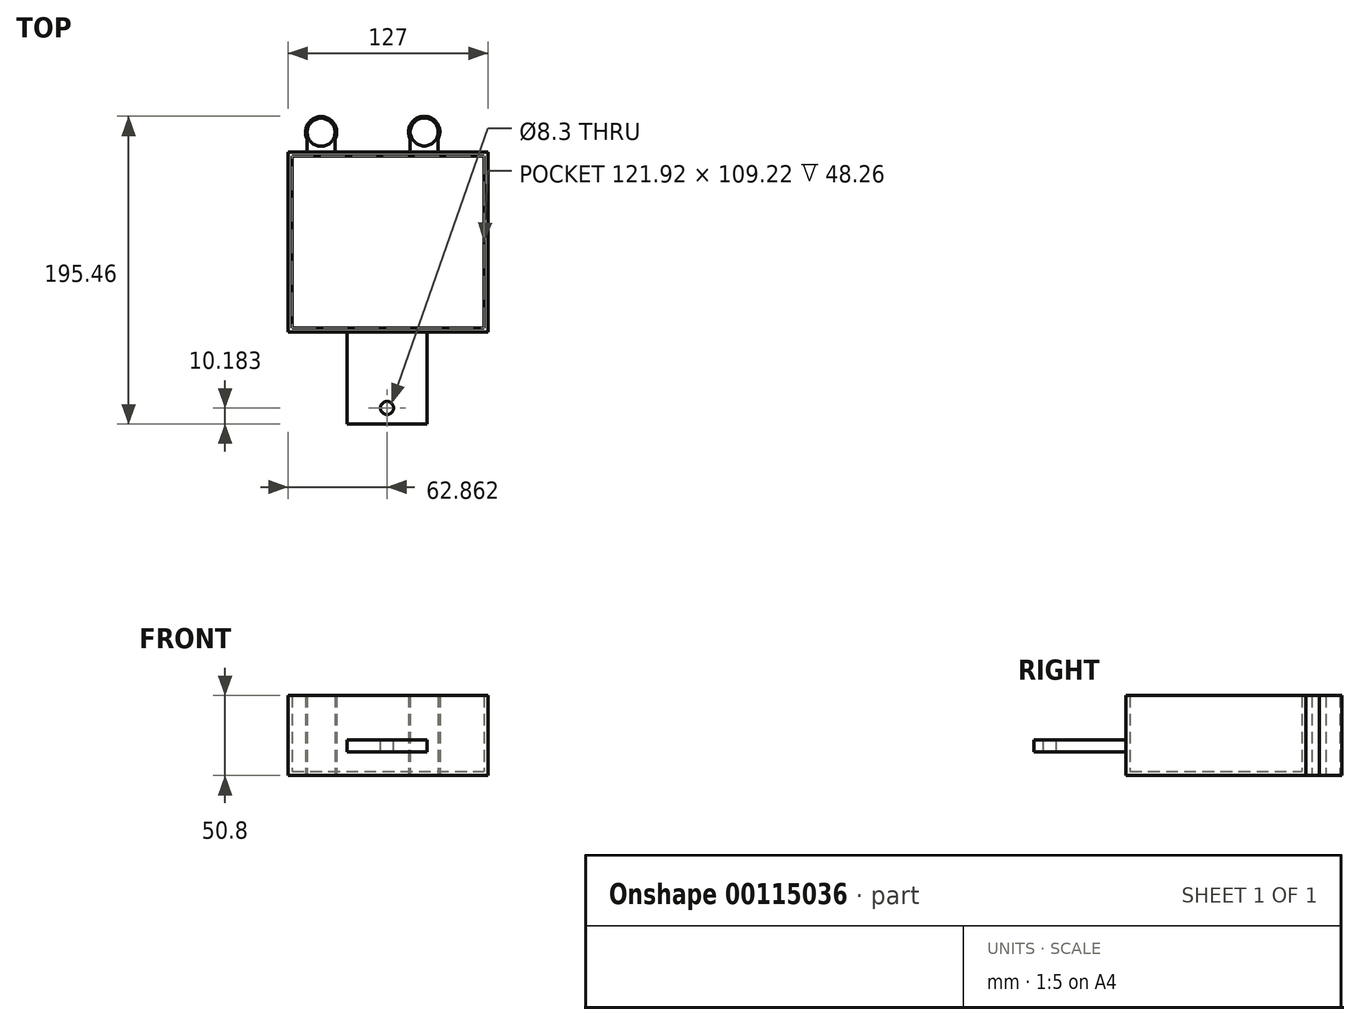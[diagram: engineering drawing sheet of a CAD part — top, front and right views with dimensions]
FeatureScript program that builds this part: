
annotation { "Feature Type Name" : "Feature", "Feature Type Description" : "" }
export const myFeature = defineFeature(function(context is Context, id is Id, definition is map)
    precondition{}
    {
        {
            var Q0;
            Q0=qCreatedBy(makeId("Top.planeOp"),FACE);
            var sketch = newSketch(context, id + "F0", { "sketchPlane" : qUnion([Q0])});
            skLineSegment(sketch, "E0.bottom", {"start": v(-61.62, -54.72) * mm, "end": v(65.38, -54.72) * mm});
            skLineSegment(sketch, "E0.top", {"start": v(-61.62, 59.58) * mm, "end": v(65.38, 59.58) * mm});
            skLineSegment(sketch, "E0.left", {"start": v(-61.62, -54.72) * mm, "end": v(-61.62, 59.58) * mm});
            skLineSegment(sketch, "E0.right", {"start": v(65.38, -54.72) * mm, "end": v(65.38, 59.58) * mm});
            skCircle(sketch, "E1", {"center": v(-40.63, 72.19) * mm, "radius": 8.9 * mm});
            skLineSegment(sketch, "E2", {"start": v(-49.52, 72.19) * mm, "end": v(-49.52, 59.58) * mm});
            skLineSegment(sketch, "E3", {"start": v(-31.74, 72.19) * mm, "end": v(-31.74, 59.58) * mm});
            skCircle(sketch, "E4", {"center": v(24.87, 72.4) * mm, "radius": 8.9 * mm});
            skLineSegment(sketch, "E5", {"start": v(33.76, 72.4) * mm, "end": v(33.76, 59.58) * mm});
            skLineSegment(sketch, "E6", {"start": v(15.98, 72.4) * mm, "end": v(15.98, 59.58) * mm});
            skCircle(sketch, "E7", {"center": v(-40.63, 72.19) * mm, "radius": 9.93 * mm});
            skCircle(sketch, "E8", {"center": v(24.87, 72.4) * mm, "radius": 9.92 * mm});
            skSolve(sketch);
        }
        {
            var Q0;
            Q0=makeQuery(id+"F0.imprint","IMPRINT",FACE,{"disambiguationData":[TD([[makeQuery(id+"F0.imprint","IMPRINT",EDGE,{"derivedFrom":sQuery(id+"F0.wireOp",EDGE,"E0.bottom")}),1.0]])]});
            extrude(context, id + "F1", {"entities" : qUnion([Q0]), "depth" : 50.8 * mm});
        }
        {
            var Q0;
            {var subQ0=sQuery(id+"F0.wireOp",EDGE,"E2");Q0=makeQuery(id+"F0.imprint","IMPRINT",FACE,{"disambiguationData":[TD([[makeQuery(id+"F0.imprint","IMPRINT",EDGE,{"derivedFrom":subQ0}),1.0]])]});}
            var Q1;
            {var subQ0=sQuery(id+"F0.wireOp",EDGE,"E5");Q1=makeQuery(id+"F0.imprint","IMPRINT",FACE,{"disambiguationData":[TD([[makeQuery(id+"F0.imprint","IMPRINT",EDGE,{"derivedFrom":subQ0}),-1.0]])]});}
            var Q2;
            Q2=sQuery(id+"F0.wireOp",EDGE,"E2");
            var Q3;
            Q3=sQuery(id+"F0.wireOp",EDGE,"E1");
            var Q4;
            Q4=sQuery(id+"F0.wireOp",EDGE,"E3");
            var Q5;
            Q5=sQuery(id+"F0.wireOp",EDGE,"E6");
            var Q6;
            Q6=sQuery(id+"F0.wireOp",EDGE,"E5");
            var Q7;
            Q7=sQuery(id+"F0.wireOp",EDGE,"E4");
            extrude(context, id + "F2", {"entities" : qUnion([Q0, Q1]), "surfaceEntities" : qUnion([Q2, Q3, Q4, Q5, Q6, Q7]), "depth" : 50.8 * mm});
        }
        {
            var Q0;
            {var subQ0=sQuery(id+"F0.wireOp",EDGE,"E2");var subQ1=sQuery(id+"F0.wireOp",EDGE,"E1");var subQ2=makeQuery(id+"F0.imprint","INTERSECT",VERTEX,{"derivedFrom":[subQ1,subQ0]});Q0=makeQuery(id+"F0.imprint","IMPRINT",FACE,{"disambiguationData":[TD([[makeQuery(id+"F0.imprint","IMPRINT",EDGE,{"disambiguationData":[TD([[subQ2,1.0]])],"derivedFrom":subQ1}),-1.0]])]});}
            var Q1;
            {var subQ0=sQuery(id+"F0.wireOp",EDGE,"E5");var subQ1=sQuery(id+"F0.wireOp",EDGE,"E4");var subQ2=makeQuery(id+"F0.imprint","INTERSECT",VERTEX,{"derivedFrom":[subQ1,subQ0]});Q1=makeQuery(id+"F0.imprint","IMPRINT",FACE,{"disambiguationData":[TD([[makeQuery(id+"F0.imprint","IMPRINT",EDGE,{"disambiguationData":[TD([[subQ2,-1.0]])],"derivedFrom":subQ1}),-1.0]])]});}
            extrude(context, id + "F3", {"entities" : qUnion([Q0, Q1]), "depth" : 50.8 * mm});
        }
        {
            var Q0;
            Q0=makeQuery(id+"F1.opExtrude","CAP_FACE",FACE,{"disambiguationData":[OSD([sQuery(id+"F0.wireOp",EDGE,"E0.bottom"),sQuery(id+"F0.wireOp",EDGE,"E0.top"),sQuery(id+"F0.wireOp",EDGE,"E0.left"),sQuery(id+"F0.wireOp",EDGE,"E0.right")])],"isStart":false});
            shell(context, id + "F4", {"entities" : qUnion([Q0]), "thickness" : 2.54 * mm});
        }
        {
            var Q0;
            Q0=makeQuery(id+"F1.opExtrude","SWEPT_FACE",FACE,{"disambiguationData":[OSD([sQuery(id+"F0.wireOp",EDGE,"E0.bottom")])]});
            var sketch = newSketch(context, id + "F5", { "sketchPlane" : qUnion([Q0])});
            skLineSegment(sketch, "E9.bottom", {"start": v(-24.16, 15.07) * mm, "end": v(26.64, 15.07) * mm});
            skLineSegment(sketch, "E9.top", {"start": v(-24.16, 22.7) * mm, "end": v(26.64, 22.7) * mm});
            skLineSegment(sketch, "E9.left", {"start": v(-24.16, 15.07) * mm, "end": v(-24.16, 22.7) * mm});
            skLineSegment(sketch, "E9.right", {"start": v(26.64, 15.07) * mm, "end": v(26.64, 22.7) * mm});
            skSolve(sketch);
        }
        {
            var Q0;
            Q0=makeQuery(id+"F5.imprint","IMPRINT",FACE,{"disambiguationData":[TD([[makeQuery(id+"F5.imprint","IMPRINT",EDGE,{"derivedFrom":sQuery(id+"F5.wireOp",EDGE,"E9.bottom")}),1.0]])]});
            extrude(context, id + "F6", {"entities" : qUnion([Q0]), "operationType" : NewBodyOperationType.ADD, "depth" : 58.42 * mm});
        }
        {
            var Q0;
            Q0=makeQuery(id+"F6.opExtrude","SWEPT_FACE",FACE,{"disambiguationData":[OSD([sQuery(id+"F5.wireOp",EDGE,"E9.top")])]});
            var sketch = newSketch(context, id + "F7", { "sketchPlane" : qUnion([Q0])});
            skCircle(sketch, "E10", {"center": v(1.24, -102.96) * mm, "radius": 4.15 * mm});
            skPoint(sketch, "E10.centerSnap0", {"position": v(1.24, -113.14) * mm});
            skSolve(sketch);
        }
        {
            var Q0;
            Q0=makeQuery(id+"F7.imprint","IMPRINT",FACE,{"disambiguationData":[TD([[makeQuery(id+"F7.imprint","IMPRINT",EDGE,{"derivedFrom":sQuery(id+"F7.wireOp",EDGE,"E10")}),1.0]])]});
            extrude(context, id + "F8", {"entities" : qUnion([Q0]), "operationType" : NewBodyOperationType.REMOVE, "oppositeDirection" : true, "depth" : 25.4 * mm});
        }
    });
